# Revit family: Sink-Bubbler_Basin-Drop_In-Acorn-CDDRB-3717_Series
name_source: partatom
category: Plumbing Fixtures
units: mm (PartAtom-declared; Revit-internal decimal feet)

## family parameters
Cut with Voids When Loaded = No
Host = Face
OmniClass Number = 23.45.05.14.14
OmniClass Title = Sinks/Lavatories
Part Type = Normal
Room Calculation Point = No
Round Connector Dimension = Use Diameter
Shared = Yes

## types (5) — shared parameters
-80 Classroom Sink, Right Bubbler, 8” Left Sink Bowl = Yes
Assembly Code = D2010440
Bubbler Basin Depth = 3 1/2"
Bubbler Basin Length = 12"
Bubbler Basin Width = 9 1/4"
CW Connection = No
CWFU = 3
Compliance Certifications = ASME A112.19.3/CSA B45.4, IAPMO® Certified for Conformance with Uniform Plumbing Code (UPC ), International Plumbing Code (IPC ), National Plumbing Code of Canada (NPC )
Default Elevation = 34"
Description = Acorn-Sinks® Stainless Steel ADA Drop-In Classroom Sink, 37" x 17"
Drain Size = 2"
Finish = Stainless Steel-18 Gauge-Type 304-Acorn-Satin
HW Connection = No
HWFU = 3
Installation Type = Drop-In Counter
Length = 17"
Manufacturer = Acorn
Product Documentation Link = https://www.acorneng.com
Product Page URL = https://www.acorneng.com
Sink Bowl Depth = 8"
Sink Bowl Length = 11 1/2"
Sink Bowl Width = 16"
URL = https://www.acorneng.com
Vent Connection = No
WFU = 4
Waste Connection = No
Width = 37 1/4"
cUPC Compliant = Yes

## per-type parameters (varying)
| type | -0 Blank, No Deck Punching | -1 | -1 Single Hole Centered | -2 | -2 2 Holes on 4” Centers (4” Centerset) | -2R | -2R Single Hole Centered w/ 2nd Hole 4” to Right | -3 | -3 3 Holes on 4” Centers (8” Centerset) |
| CDDRB-3717-0 | Yes | 1/2" | No | 9 1/2" | No | 1/2" | No | 1/2" | No |
| CDDRB-3717-1 | No | 0" | Yes | 9 1/2" | No | 1/2" | No | 1/2" | No |
| CDDRB-3717-2 | No | 0" | No | 7 1/2" | Yes | 0" | No | 1/2" | No |
| CDDRB-3717-2R | No | 0" | No | 9 1/2" | No | 0" | Yes | 1/2" | No |
| CDDRB-3717-3 | No | 0" | No | 9 1/2" | No | 0" | No | 0" | Yes |

note: column(s) folded — value = type name in every type: Model

## geometry (parser evidence)
native form markers: Sweep x3
no freeform markers — native parametric forms only
